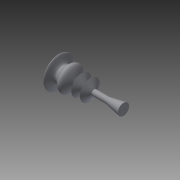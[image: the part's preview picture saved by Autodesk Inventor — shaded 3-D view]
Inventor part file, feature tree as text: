
AUTODESK INVENTOR PART (.ipt)
format: ipt  version: 2015 (Build 190159000, 159)  size: 139,264 bytes
history: native  units: in
note: dims shown in document units (in); Inventor stores cm internally (conversion verified against a paired STEP export)
features: revolve x1, sketch x1
ambient origin geometry x8: Origin, YZ Plane, XZ Plane, XY Plane, X Axis, Y Axis, Z Axis, Center Point
bodies: Solid1 (feature_tree)
feature tree (2):
  revolve  "Revolution1"  [1 undecoded]
  sketch  "Sketch1"  dims[d0=0.5in d1=0.0421in d2=90.0deg]
note: 1 required parameter value undecoded (feature->parameter linkage not recoverable at this tier; creation-order binding heuristic only, values carry confidence <= 0.55)
